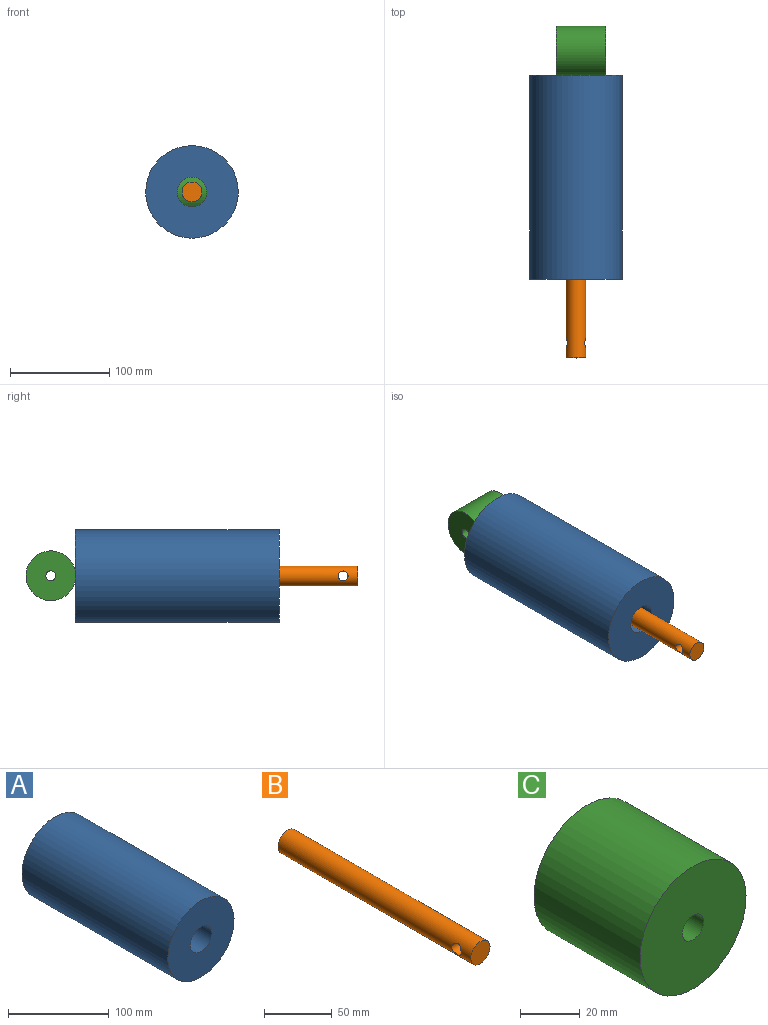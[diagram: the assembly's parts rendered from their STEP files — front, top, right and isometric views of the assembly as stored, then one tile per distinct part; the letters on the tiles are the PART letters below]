
ASSEMBLY  parts=3 mates=1
PART A: 4 faces, bbox 93x205x93 mm
  f0: cylinder r=46.5mm len=205mm, axis (0,1,0), area 59894.5mm2, adj f1,f2
  f1: plane 93x93mm, normal (0,-1,0), area 6086.1mm2, adj f0,f3
  f2: plane 93x93mm, normal (0,1,0), area 6086.1mm2, adj f0,f3
  f3: cylinder r=15mm len=205mm, axis (0,1,0), area 19320.8mm2, adj f1,f2
PART B: 4 faces, bbox 20x201x20 mm
  f0: cylinder r=10mm len=201mm, axis (0,1,0), area 12467mm2, adj f1,f2,f3
  f1: plane 20x20mm, normal (0,-1,0), area 314.2mm2, adj f0
  f2: plane 20x20mm, normal (0,1,0), area 314.2mm2, adj f0
  f3: cylinder r=5mm len=20mm, axis (-1,0,0), area 587mm2, adj f0
PART C: 4 faces, bbox 50x50x50 mm
  f0: cylinder r=5mm len=50mm, axis (0,1,0), area 1570.8mm2, adj f2,f3
  f1: cylinder r=25mm len=50mm, axis (0,1,0), area 7854mm2, adj f2,f3
  f2: plane 50x50mm, normal (0,-1,0), area 1885mm2, adj f0,f1
  f3: plane 50x50mm, normal (0,1,0), area 1885mm2, adj f0,f1
PLACE A t=(-106.24,24.94,-12.34)mm
PLACE B t=(-106.24,-58.36,-12.34)mm
PLACE C rot(axis=(0,0,1),90deg) t=(-126.35,49.71,-12.16)mm
MATE cylindrical B.f0 <-> A.f3  axis (0,1,0) through (-106.24,-158.86,-12.34)mm
